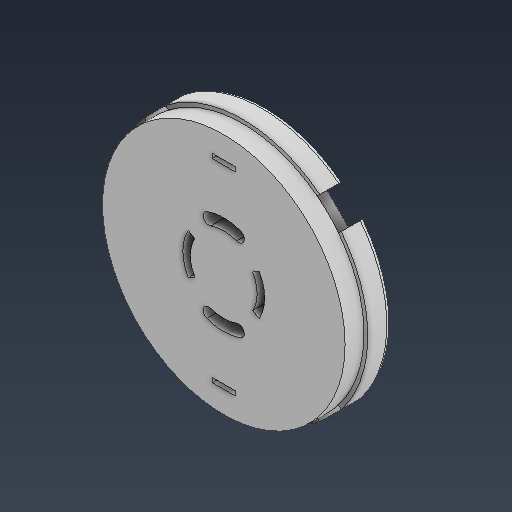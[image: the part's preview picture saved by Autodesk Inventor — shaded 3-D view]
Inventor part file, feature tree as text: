
AUTODESK INVENTOR PART (.ipt)
format: ipt  version: 2021 (Build 250183000, 183)  size: 203,264 bytes
history: native  units: in
note: dims shown in document units (in); Inventor stores cm internally (conversion verified against a paired STEP export)
features: fillet x1
ambient origin geometry x8: Origin, YZ Plane, XZ Plane, XY Plane, X Axis, Y Axis, Z Axis, Center Point
bodies: Solid1 (feature_tree)
feature tree (1):
  fillet  "Fillet2"  [1 undecoded]
note: 1 required parameter value undecoded (feature->parameter linkage not recoverable at this tier; creation-order binding heuristic only, values carry confidence <= 0.55)
